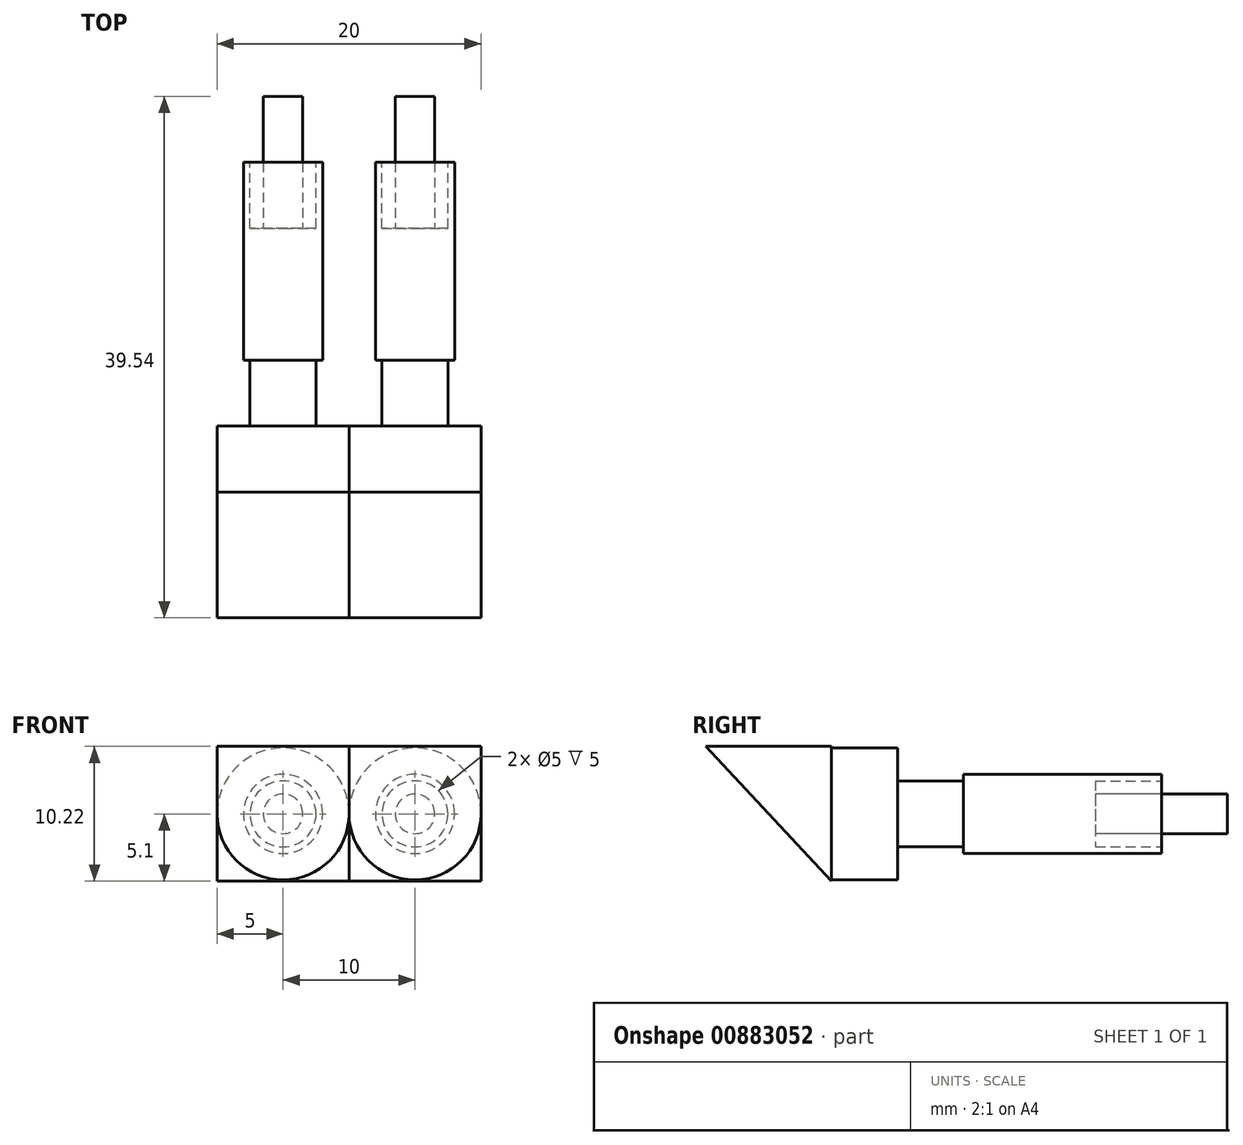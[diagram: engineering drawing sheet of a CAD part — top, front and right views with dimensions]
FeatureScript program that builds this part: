
annotation { "Feature Type Name" : "Feature", "Feature Type Description" : "" }
export const myFeature = defineFeature(function(context is Context, id is Id, definition is map)
    precondition{}
    {
        {
            var Q0;
            Q0=qCreatedBy(makeId("Front.planeOp"),FACE);
            var sketch = newSketch(context, id + "F0", { "sketchPlane" : qUnion([Q0])});
            skCircle(sketch, "E0", {"center": v(5, 0) * mm, "radius": 5 * mm});
            skCircle(sketch, "E1", {"center": v(-5, 0) * mm, "radius": 5 * mm});
            skSolve(sketch);
        }
        {
            var Q0;
            Q0 = qSketchRegion(id + "F0", true);
            extrude(context, id + "F1", {"entities" : qUnion([Q0]), "oppositeDirection" : true, "depth" : 5 * mm, "offsetDistance" : 25 * mm});
        }
        {
            var Q0;
            Q0=makeQuery(id+"F1.opExtrude","CAP_FACE",FACE,{"disambiguationData":[OSD([sQuery(id+"F0.wireOp",EDGE,"E1")])],"isStart":false});
            var sketch = newSketch(context, id + "F2", { "sketchPlane" : qUnion([Q0])});
            skCircle(sketch, "E2", {"center": v(-5, 0) * mm, "radius": 2.5 * mm});
            skCircle(sketch, "E3", {"center": v(5, 0) * mm, "radius": 2.5 * mm});
            skSolve(sketch);
        }
        {
            var Q0;
            Q0 = qSketchRegion(id + "F2", true);
            extrude(context, id + "F3", {"entities" : qUnion([Q0]), "operationType" : NewBodyOperationType.ADD, "depth" : 15 * mm, "offsetDistance" : 25 * mm});
        }
        {
            var Q0;
            Q0=makeQuery(id+"F3.opExtrude","CAP_FACE",FACE,{"disambiguationData":[OSD([sQuery(id+"F2.wireOp",EDGE,"E2")])],"isStart":false});
            var sketch = newSketch(context, id + "F4", { "sketchPlane" : qUnion([Q0])});
            skCircle(sketch, "E4", {"center": v(-5, 0) * mm, "radius": 2.5 * mm});
            skCircle(sketch, "E5", {"center": v(-5, 0) * mm, "radius": 3 * mm});
            skCircle(sketch, "E6", {"center": v(5, 0) * mm, "radius": 2.5 * mm});
            skCircle(sketch, "E7", {"center": v(5, 0) * mm, "radius": 3 * mm});
            skSolve(sketch);
        }
        {
            var Q0;
            Q0=makeQuery(id+"F4.imprint","IMPRINT",FACE,{"disambiguationData":[TD([[makeQuery(id+"F4.imprint","IMPRINT",EDGE,{"derivedFrom":sQuery(id+"F4.wireOp",EDGE,"E4")}),-1.0]])]});
            var Q1;
            Q1=makeQuery(id+"F4.imprint","IMPRINT",FACE,{"disambiguationData":[TD([[makeQuery(id+"F4.imprint","IMPRINT",EDGE,{"derivedFrom":sQuery(id+"F4.wireOp",EDGE,"E6")}),-1.0]])]});
            extrude(context, id + "F5", {"entities" : qUnion([Q0, Q1]), "oppositeDirection" : true, "depth" : 10 * mm, "offsetDistance" : 25 * mm});
        }
        {
            var Q0;
            Q0=makeQuery(id+"F5.opExtrude","CAP_FACE",FACE,{"disambiguationData":[OSD([sQuery(id+"F4.wireOp",EDGE,"E4"),sQuery(id+"F4.wireOp",EDGE,"E5")])],"isStart":true});
            var Q1;
            Q1=makeQuery(id+"F5.opExtrude","CAP_FACE",FACE,{"disambiguationData":[OSD([sQuery(id+"F4.wireOp",EDGE,"E6"),sQuery(id+"F4.wireOp",EDGE,"E7")])],"isStart":true});
            extrude(context, id + "F6", {"entities" : qUnion([Q0, Q1]), "operationType" : NewBodyOperationType.ADD, "depth" : 5 * mm, "offsetDistance" : 25 * mm});
        }
        {
            var Q0;
            Q0=makeQuery(id+"F3.opExtrude","CAP_FACE",FACE,{"disambiguationData":[OSD([sQuery(id+"F2.wireOp",EDGE,"E2")])],"isStart":false});
            var sketch = newSketch(context, id + "F7", { "sketchPlane" : qUnion([Q0])});
            skCircle(sketch, "E8", {"center": v(-5, 0) * mm, "radius": 1.5 * mm});
            skCircle(sketch, "E9", {"center": v(5, 0) * mm, "radius": 1.5 * mm});
            skSolve(sketch);
        }
        {
            var Q0;
            Q0 = qSketchRegion(id + "F7", true);
            extrude(context, id + "F8", {"entities" : qUnion([Q0]), "operationType" : NewBodyOperationType.ADD, "depth" : 10 * mm, "offsetDistance" : 25 * mm});
        }
        {
            var Q0;
            Q0=makeQuery(id+"F8.opExtrude","CAP_FACE",FACE,{"disambiguationData":[OSD([sQuery(id+"F7.wireOp",EDGE,"E8")])],"isStart":false});
            var sketch = newSketch(context, id + "F9", { "sketchPlane" : qUnion([Q0])});
            skCircle(sketch, "E10", {"center": v(-5, 0) * mm, "radius": 1 * mm});
            skCircle(sketch, "E11", {"center": v(5, 0) * mm, "radius": 1 * mm});
            skSolve(sketch);
        }
        {
            var Q0;
            Q0 = qSketchRegion(id + "F9", true);
            extrude(context, id + "F10", {"entities" : qUnion([Q0]), "operationType" : NewBodyOperationType.ADD, "oppositeDirection" : true, "depth" : 10 * mm, "offsetDistance" : 25 * mm});
        }
        {
            var Q0;
            Q0=qCreatedBy(makeId("Front.planeOp"),FACE);
            var sketch = newSketch(context, id + "F11", { "sketchPlane" : qUnion([Q0])});
            skPoint(sketch, "E12.middle", {"position": v(0, 0) * mm});
            skLineSegment(sketch, "E13.bottom", {"start": v(0, 5) * mm, "end": v(10, 5) * mm});
            skLineSegment(sketch, "E13.top", {"start": v(0, -5) * mm, "end": v(10, -5) * mm});
            skLineSegment(sketch, "E13.left", {"start": v(0, 5) * mm, "end": v(0, -5) * mm});
            skLineSegment(sketch, "E13.right", {"start": v(10, 5) * mm, "end": v(10, -5) * mm});
            skPoint(sketch, "E13.middle", {"position": v(5, 0) * mm});
            skLineSegment(sketch, "E14.bottom", {"start": v(-10, 5) * mm, "end": v(0, 5) * mm});
            skLineSegment(sketch, "E14.top", {"start": v(-10, -5) * mm, "end": v(0, -5) * mm});
            skLineSegment(sketch, "E14.left", {"start": v(-10, 5) * mm, "end": v(-10, -5) * mm});
            skPoint(sketch, "E14.middle", {"position": v(-5, 0) * mm});
            skSolve(sketch);
        }
        {
            var Q0;
            Q0 = qSketchRegion(id + "F11", true);
            extrude(context, id + "F12", {"entities" : qUnion([Q0]), "depth" : 0.1 * mm, "offsetDistance" : 25 * mm});
        }
        {
            var Q0;
            Q0 = qSketchRegion(id + "F11", true);
            extrude(context, id + "F13", {"entities" : qUnion([Q0]), "depth" : 0.1 * mm, "offsetDistance" : 25 * mm});
        }
        {
            var Q0;
            Q0=makeQuery(id+"F12.opExtrude","SWEPT_BODY",BODY,{"disambiguationData":[OSD([sQuery(id+"F11.wireOp",EDGE,"E13.bottom"),sQuery(id+"F11.wireOp",EDGE,"E13.top"),sQuery(id+"F11.wireOp",EDGE,"E13.right"),sQuery(id+"F11.wireOp",EDGE,"E14.bottom"),sQuery(id+"F11.wireOp",EDGE,"E14.top"),sQuery(id+"F11.wireOp",EDGE,"E14.left")])]});
            var Q1;
            Q1=makeQuery(id+"F13.opExtrude","SWEPT_BODY",BODY,{"disambiguationData":[OSD([sQuery(id+"F11.wireOp",EDGE,"E13.bottom"),sQuery(id+"F11.wireOp",EDGE,"E13.top"),sQuery(id+"F11.wireOp",EDGE,"E13.right"),sQuery(id+"F11.wireOp",EDGE,"E14.bottom"),sQuery(id+"F11.wireOp",EDGE,"E14.top"),sQuery(id+"F11.wireOp",EDGE,"E14.left")])]});
            deleteBodies(context, id + "F14", {"entities" : qUnion([Q0, Q1])});
        }
        {
            var Q0;
            Q0=qCreatedBy(makeId("Right.planeOp"),FACE);
            var sketch = newSketch(context, id + "F15", { "sketchPlane" : qUnion([Q0])});
            skLineSegment(sketch, "E15", {"start": v(0, 5.12) * mm, "end": v(-9.54, 5.12) * mm});
            skLineSegment(sketch, "E16", {"start": v(-9.54, 5.12) * mm, "end": v(0, -5.1) * mm});
            skLineSegment(sketch, "E17", {"start": v(0, -5.1) * mm, "end": v(0, 5.12) * mm});
            skSolve(sketch);
        }
        {
            var Q0;
            Q0 = qSketchRegion(id + "F15", true);
            extrude(context, id + "F16", {"entities" : qUnion([Q0]), "depth" : 10 * mm, "offsetDistance" : 25 * mm});
        }
        {
            var Q0;
            Q0=makeQuery(id+"F16.opExtrude","CAP_FACE",FACE,{"disambiguationData":[OSD([sQuery(id+"F15.wireOp",EDGE,"E15"),sQuery(id+"F15.wireOp",EDGE,"E16"),sQuery(id+"F15.wireOp",EDGE,"E17")])],"isStart":true});
            extrude(context, id + "F17", {"entities" : qUnion([Q0]), "depth" : 10 * mm, "offsetDistance" : 25 * mm});
        }
    });
